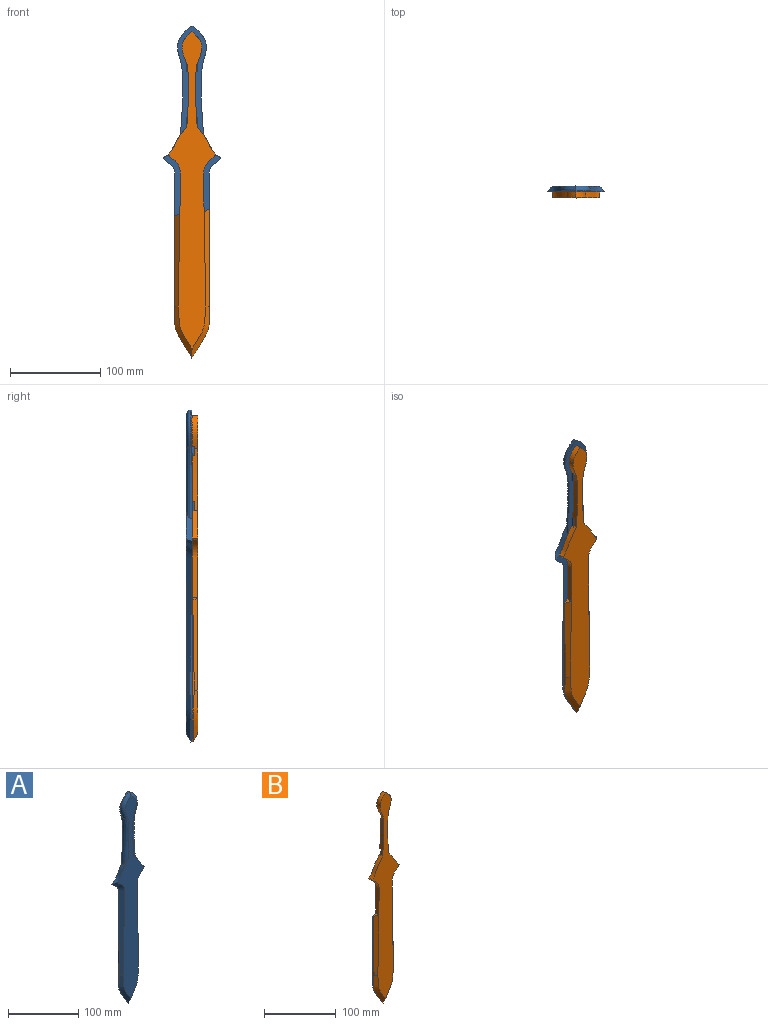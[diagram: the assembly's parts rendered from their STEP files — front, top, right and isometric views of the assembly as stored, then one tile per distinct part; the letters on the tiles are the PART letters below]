
ASSEMBLY  parts=2 mates=1
PART A: 43 faces, bbox 65.8x10.3x372 mm
  f0: extruded ~34.6x26mm, area 220.3mm2, adj f8,f9,f12,f15
  f1: plane 165.11x2.58mm, normal (-1,0,0), area 224.8mm2, adj f2,f9,f10,f12
  f2: extruded ~38.1x19.05mm, area 54.6mm2, adj f1,f3,f9,f10
  f3: extruded ~38.1x19.05mm, area 54.6mm2, adj f2,f4,f9,f11
  f4: plane 165.11x2.58mm, normal (1,0,0), area 224.7mm2, adj f3,f9,f11,f13
  f5: extruded ~34.6x26mm, area 220.3mm2, adj f8,f9,f13,f14
  f6: extruded ~38.82x15.97mm, area 57.2mm2, adj f7,f9,f14,f16
  f7: extruded ~38.82x15.97mm, area 57.2mm2, adj f6,f9,f15,f17
  f8: plane 353.46x55.48mm, normal (0,-1,0), area 8085.1mm2, adj f0,f5,f10,f11,f12,f13,f14,f15
  f9: plane 368.3x63.5mm, normal (0,1,0), area 11034.2mm2, adj f0,f1,f2,f3,f4,f5,f6,f7
  f10: bspline ~78.42x26.66mm, area 391.5mm2, adj f1,f2,f8,f11,f12
  f11: bspline ~57.87x24.8mm, area 390.7mm2, adj f3,f4,f8,f10,f13
  f12: bspline ~168.43x19.44mm, area 1275.1mm2, adj f0,f1,f8,f9,f10
  f13: bspline ~170.41x19.62mm, area 1274.4mm2, adj f4,f5,f8,f9,f11
  f14: bspline ~105.56x10.17mm, area 767.8mm2, adj f5,f6,f8,f9,f16
  f15: bspline ~105.56x10.17mm, area 767.7mm2, adj f0,f7,f8,f9,f17
  f16: bspline ~54.86x20.83mm, area 353.4mm2, adj f6,f8,f14,f17
  f17: bspline ~54.86x20.82mm, area 353.4mm2, adj f7,f8,f15,f16
  f18: plane 12.7x2.54mm, normal (0,0,1), area 32.3mm2, adj f9,f19,f21,f22
  f19: plane 12.7x2.54mm, normal (1,0,0), area 32.3mm2, adj f9,f18,f20,f22
  f20: plane 12.7x2.54mm, normal (0,0,-1), area 32.3mm2, adj f9,f19,f21,f22
  f21: plane 12.7x2.54mm, normal (-1,0,0), area 32.3mm2, adj f9,f18,f20,f22
  f22: plane 12.7x12.7mm, normal (0,1,0), area 161.3mm2, adj f18,f19,f20,f21
  f23: plane 12.7x2.54mm, normal (0,0,1), area 32.3mm2, adj f9,f24,f26,f27
  f24: plane 12.7x2.54mm, normal (1,0,0), area 32.3mm2, adj f9,f23,f25,f27
  f25: plane 12.7x2.54mm, normal (0,0,-1), area 32.3mm2, adj f9,f24,f26,f27
  f26: plane 12.7x2.54mm, normal (-1,0,0), area 32.3mm2, adj f9,f23,f25,f27
  f27: plane 12.7x12.7mm, normal (0,1,0), area 161.3mm2, adj f23,f24,f25,f26
  f28: plane 12.7x2.54mm, normal (0,0,1), area 32.3mm2, adj f9,f29,f31,f32
  f29: plane 12.7x2.54mm, normal (1,0,0), area 32.3mm2, adj f9,f28,f30,f32
  f30: plane 12.7x2.54mm, normal (0,0,-1), area 32.3mm2, adj f9,f29,f31,f32
  f31: plane 12.7x2.54mm, normal (-1,0,0), area 32.3mm2, adj f9,f28,f30,f32
  f32: plane 12.7x12.7mm, normal (0,1,0), area 161.3mm2, adj f28,f29,f30,f31
  f33: plane 12.7x2.54mm, normal (0,0,1), area 32.3mm2, adj f9,f34,f36,f37
  f34: plane 12.7x2.54mm, normal (1,0,0), area 32.3mm2, adj f9,f33,f35,f37
  f35: plane 12.7x2.54mm, normal (0,0,-1), area 32.3mm2, adj f9,f34,f36,f37
  f36: plane 12.7x2.54mm, normal (-1,0,0), area 32.3mm2, adj f9,f33,f35,f37
  f37: plane 12.7x12.7mm, normal (0,1,0), area 161.3mm2, adj f33,f34,f35,f36
  f38: plane 12.7x2.54mm, normal (0,0,1), area 32.3mm2, adj f9,f39,f41,f42
  f39: plane 12.7x2.54mm, normal (1,0,0), area 32.3mm2, adj f9,f38,f40,f42
  f40: plane 12.7x2.54mm, normal (0,0,-1), area 32.3mm2, adj f9,f39,f41,f42
  f41: plane 12.7x2.54mm, normal (-1,0,0), area 32.3mm2, adj f9,f38,f40,f42
  f42: plane 12.7x12.7mm, normal (0,1,0), area 161.3mm2, adj f38,f39,f40,f41
PART B: 47 faces, bbox 55.3x7.5x364.2 mm
  f0: plane 256.05x54.1mm, normal (0,1,0), area 7874.7mm2, adj f9,f11,f12,f13,f14,f15,f16,f22
  f1: plane 50.86x10.23mm, normal (0,1,0), area 415.8mm2, adj f5,f8,f39,f41
  f2: plane 34.04x21.8mm, normal (0,1,0), area 534.8mm2, adj f4,f6,f21,f40,f42
  f3: plane 353.26x55.29mm, normal (0,-1,0), area 8054.5mm2, adj f11,f16,f17,f18,f19,f20,f39,f40
  f4: plane 2.54x2.25mm, normal (-1,0,0), area 5.7mm2, adj f2,f7,f21,f40
  f5: plane 8.78x2.54mm, normal (0,0,1), area 22.3mm2, adj f1,f7,f39,f41
  f6: plane 2.54x2.25mm, normal (1,0,0), area 5.7mm2, adj f2,f7,f21,f42
  f7: plane 12.71x12.7mm, normal (0,1,0), area 134.7mm2, adj f4,f5,f6,f21,f39,f40,f41,f42
  f8: plane 10.17x2.54mm, normal (0,0,-1), area 25.8mm2, adj f1,f10,f39,f41
  f9: plane 2.54x2.05mm, normal (1,0,0), area 5.2mm2, adj f0,f10,f11,f23
  f10: plane 12.7x12.7mm, normal (0,1,0), area 142.4mm2, adj f8,f9,f11,f16,f22,f23,f39,f41
  f11: extruded ~30.87x20.8mm, area 234.8mm2, adj f0,f3,f9,f10,f41,f46
  f12: plane 118.87x2.58mm, normal (-1,0,0), area 205.9mm2, adj f0,f13,f17,f19,f45
  f13: extruded ~38.1x19.05mm, area 54.6mm2, adj f0,f12,f14,f17
  f14: extruded ~38.1x19.05mm, area 54.6mm2, adj f0,f13,f15,f18
  f15: plane 128.03x2.58mm, normal (1,0,0), area 212.6mm2, adj f0,f14,f18,f20,f43
  f16: extruded ~30.87x20.8mm, area 234.8mm2, adj f0,f3,f10,f22,f39,f44
  f17: bspline ~78.42x26.66mm, area 391.5mm2, adj f3,f12,f13,f18,f19
  f18: bspline ~57.87x24.8mm, area 390.7mm2, adj f3,f14,f15,f17,f20
  f19: bspline ~119.42x8.46mm, area 665.5mm2, adj f3,f12,f17,f45
  f20: bspline ~119.47x8.46mm, area 708.6mm2, adj f3,f15,f18,f43
  f21: plane 12.7x2.54mm, normal (0,0,-1), area 32.3mm2, adj f2,f4,f6,f7
  f22: plane 2.54x2.05mm, normal (-1,0,0), area 5.2mm2, adj f0,f10,f16,f23
  f23: plane 12.7x2.54mm, normal (0,0,1), area 32.3mm2, adj f0,f9,f10,f22
  f24: plane 12.7x2.54mm, normal (0,0,-1), area 32.3mm2, adj f0,f25,f27,f28
  f25: plane 12.7x2.54mm, normal (-1,0,0), area 32.3mm2, adj f0,f24,f26,f28
  f26: plane 12.7x2.54mm, normal (0,0,1), area 32.3mm2, adj f0,f25,f27,f28
  f27: plane 12.7x2.54mm, normal (1,0,0), area 32.3mm2, adj f0,f24,f26,f28
  f28: plane 12.7x12.7mm, normal (0,1,0), area 161.3mm2, adj f24,f25,f26,f27
  f29: plane 12.7x2.54mm, normal (0,0,-1), area 32.3mm2, adj f0,f30,f32,f33
  f30: plane 12.7x2.54mm, normal (-1,0,0), area 32.3mm2, adj f0,f29,f31,f33
  f31: plane 12.7x2.54mm, normal (0,0,1), area 32.3mm2, adj f0,f30,f32,f33
  f32: plane 12.7x2.54mm, normal (1,0,0), area 32.3mm2, adj f0,f29,f31,f33
  f33: plane 12.7x12.7mm, normal (0,1,0), area 161.3mm2, adj f29,f30,f31,f32
  f34: plane 12.7x2.54mm, normal (0,0,-1), area 32.3mm2, adj f0,f35,f37,f38
  f35: plane 12.7x2.54mm, normal (-1,0,0), area 32.3mm2, adj f0,f34,f36,f38
  f36: plane 12.7x2.54mm, normal (0,0,1), area 32.3mm2, adj f0,f35,f37,f38
  f37: plane 12.7x2.54mm, normal (1,0,0), area 32.3mm2, adj f0,f34,f36,f38
  f38: plane 12.7x12.7mm, normal (0,1,0), area 161.3mm2, adj f34,f35,f36,f37
  f39: extruded ~68.62x6.35mm, area 391.2mm2, adj f1,f3,f5,f7,f8,f10,f16,f40
  f40: extruded ~36.51x10.89mm, area 255.9mm2, adj f2,f3,f4,f7,f39,f42
  f41: extruded ~68.62x6.35mm, area 391.2mm2, adj f1,f3,f5,f7,f8,f10,f11,f42
  f42: extruded ~36.51x10.89mm, area 255.9mm2, adj f2,f3,f6,f7,f40,f41
  f43: plane 6.35x5.62mm, normal (-0.62,0,0.78), area 25.1mm2, adj f0,f15,f20,f44
  f44: extruded ~64.32x13.84mm, area 459.6mm2, adj f0,f3,f16,f43
  f45: plane 6.35x5.59mm, normal (-0.47,0,0.88), area 22.7mm2, adj f0,f12,f19,f46
  f46: extruded ~66.04x13.84mm, area 451.1mm2, adj f0,f3,f11,f45
PLACE A rot(axis=(0,0,1),180deg) t=(-261.81,329.66,-90.61)mm
PLACE B t=(-266.6,329.66,-90.61)mm
MATE fastened A.f22 <-> B.f28  axis (0,-1,0) through (-264.2,327.12,0.4)mm
